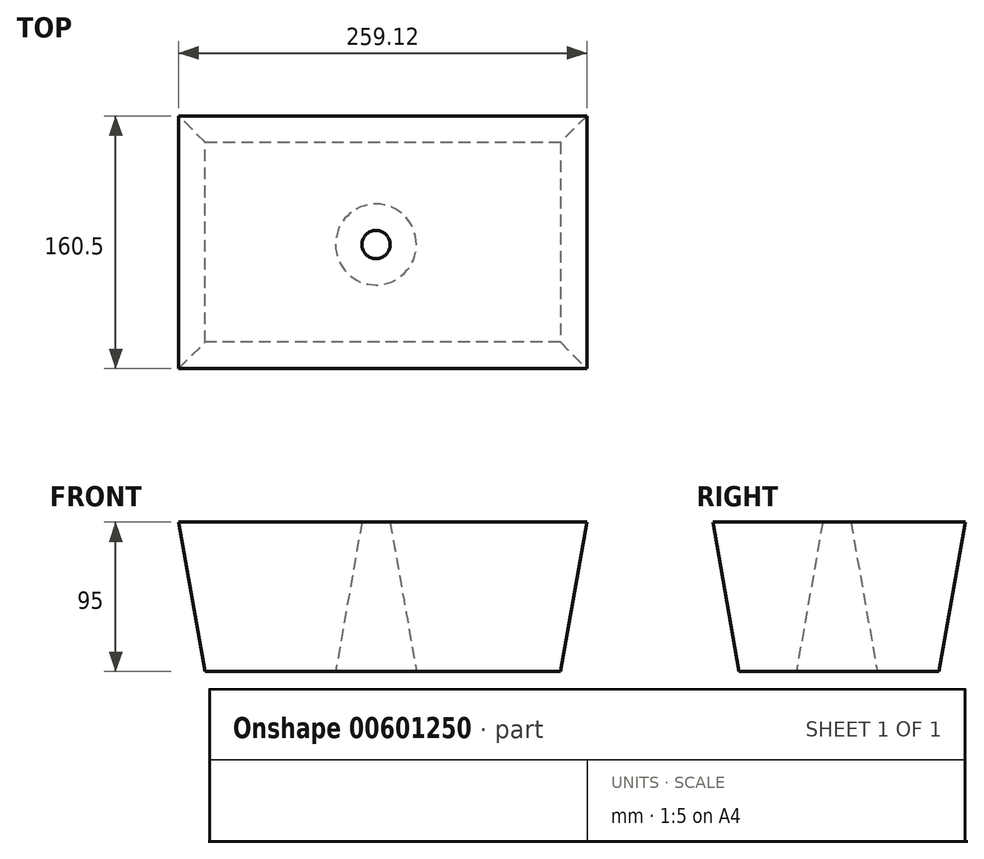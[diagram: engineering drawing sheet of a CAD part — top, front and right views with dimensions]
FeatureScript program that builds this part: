
annotation { "Feature Type Name" : "Feature", "Feature Type Description" : "" }
export const myFeature = defineFeature(function(context is Context, id is Id, definition is map)
    precondition{}
    {
        {
            var Q0;
            Q0=qCreatedBy(makeId("Top.planeOp"),FACE);
            var sketch = newSketch(context, id + "F0", { "sketchPlane" : qUnion([Q0])});
            skLineSegment(sketch, "E0.bottom", {"start": v(-89.7, 46.66) * mm, "end": v(135.92, 46.66) * mm});
            skLineSegment(sketch, "E0.top", {"start": v(-89.7, -80.34) * mm, "end": v(135.92, -80.34) * mm});
            skLineSegment(sketch, "E0.left", {"start": v(-89.7, 46.66) * mm, "end": v(-89.7, -80.34) * mm});
            skLineSegment(sketch, "E0.right", {"start": v(135.92, 46.66) * mm, "end": v(135.92, -80.34) * mm});
            skCircle(sketch, "E1", {"center": v(18.8, -18.3) * mm, "radius": 25.7 * mm});
            skSolve(sketch);
        }
        {
            var Q0;
            Q0 = qSketchRegion(id + "F0", true);
            extrude(context, id + "F1", {"entities" : qUnion([Q0]), "depth" : 95 * mm, "offsetDistance" : 25.4 * mm, "hasDraft" : true, "draftAngle" : 10 * degree});
        }
    });
